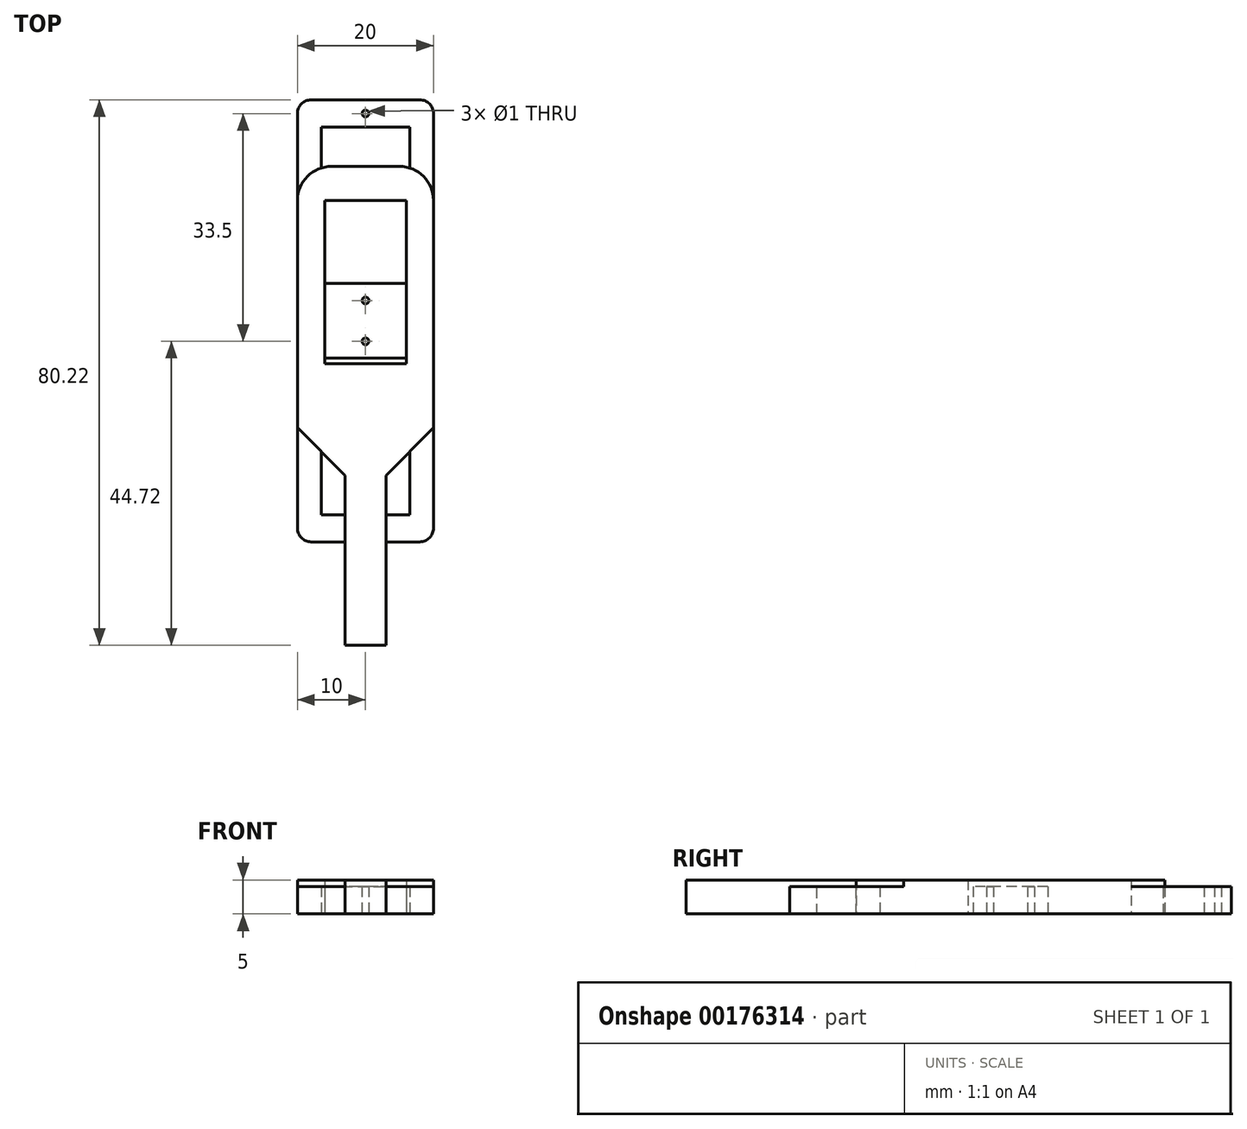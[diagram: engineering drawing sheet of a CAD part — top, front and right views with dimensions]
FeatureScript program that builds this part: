
annotation { "Feature Type Name" : "Feature", "Feature Type Description" : "" }
export const myFeature = defineFeature(function(context is Context, id is Id, definition is map)
    precondition{}
    {
        {
            var Q0;
            Q0=qCreatedBy(makeId("Top.planeOp"),FACE);
            var sketch = newSketch(context, id + "F0", { "sketchPlane" : qUnion([Q0])});
            skLineSegment(sketch, "E0.bottom", {"start": v(-10, -32.5) * mm, "end": v(10, -32.5) * mm});
            skLineSegment(sketch, "E0.top", {"start": v(-10, 32.5) * mm, "end": v(10, 32.5) * mm});
            skLineSegment(sketch, "E0.left", {"start": v(-10, -32.5) * mm, "end": v(-10, 32.5) * mm});
            skLineSegment(sketch, "E0.right", {"start": v(10, -32.5) * mm, "end": v(10, 32.5) * mm});
            skPoint(sketch, "E0.middle", {"position": v(0, 0) * mm});
            skLineSegment(sketch, "E1.bottom", {"start": v(6.5, 28.5) * mm, "end": v(-6.5, 28.5) * mm});
            skLineSegment(sketch, "E1.top", {"start": v(6.5, 5.5) * mm, "end": v(-6.5, 5.5) * mm});
            skLineSegment(sketch, "E1.left", {"start": v(6.5, 28.5) * mm, "end": v(6.5, 5.5) * mm});
            skLineSegment(sketch, "E1.right", {"start": v(-6.5, 28.5) * mm, "end": v(-6.5, 5.5) * mm});
            skPoint(sketch, "E1.middle", {"position": v(0, 17) * mm});
            skLineSegment(sketch, "E2.MirrorCS", {"start": v(6.5, -28.5) * mm, "end": v(-6.5, -28.5) * mm});
            skLineSegment(sketch, "E3.MirrorCS", {"start": v(-6.5, -28.5) * mm, "end": v(-6.5, -5.5) * mm});
            skLineSegment(sketch, "E4.MirrorCS", {"start": v(6.5, -28.5) * mm, "end": v(6.5, -5.5) * mm});
            skLineSegment(sketch, "E5.MirrorCS", {"start": v(6.5, -5.5) * mm, "end": v(-6.5, -5.5) * mm});
            skPoint(sketch, "E6", {"position": v(0, 30.5) * mm});
            skPoint(sketch, "E7", {"position": v(0, 3) * mm});
            skPoint(sketch, "E8", {"position": v(0, -3) * mm});
            skPoint(sketch, "E9", {"position": v(0, -30.5) * mm});
            skPoint(sketch, "E9.positionSnap0", {"position": v(0, -32.5) * mm});
            skCircle(sketch, "E10", {"center": v(0, 30.5) * mm, "radius": 0.5 * mm});
            skCircle(sketch, "E11", {"center": v(0, -30.5) * mm, "radius": 0.5 * mm});
            skCircle(sketch, "E12", {"center": v(0, 3) * mm, "radius": 0.5 * mm});
            skCircle(sketch, "E13", {"center": v(0, -3) * mm, "radius": 0.5 * mm});
            skSolve(sketch);
        }
        {
            var Q0;
            Q0=qSketchRegion(id+"F0",true);
            extrude(context, id + "F1", {"entities" : qUnion([Q0]), "depth" : 4 * mm});
        }
        {
            var Q0;
            Q0=makeQuery(id+"F1.opExtrude","SWEPT_EDGE",EDGE,{"disambiguationData":[OSD([sQuery(id+"F0.wireOp",EDGE,"E0.bottom"),sQuery(id+"F0.wireOp",EDGE,"E0.right")])]});
            var Q1;
            Q1=makeQuery(id+"F1.opExtrude","SWEPT_EDGE",EDGE,{"disambiguationData":[OSD([sQuery(id+"F0.wireOp",EDGE,"E0.top"),sQuery(id+"F0.wireOp",EDGE,"E0.right")])]});
            var Q2;
            Q2=makeQuery(id+"F1.opExtrude","SWEPT_EDGE",EDGE,{"disambiguationData":[OSD([sQuery(id+"F0.wireOp",EDGE,"E0.bottom"),sQuery(id+"F0.wireOp",EDGE,"E0.left")])]});
            var Q3;
            Q3=makeQuery(id+"F1.opExtrude","SWEPT_EDGE",EDGE,{"disambiguationData":[OSD([sQuery(id+"F0.wireOp",EDGE,"E0.top"),sQuery(id+"F0.wireOp",EDGE,"E0.left")])]});
            fillet(context, id + "F2", {"entities" : qUnion([Q0, Q1, Q2, Q3]), "radius" : 2 * mm, "tangentPropagation" : true, "allowEdgeOverflow" : false});
        }
        {
            var Q0;
            Q0=qCreatedBy(makeId("Top.planeOp"),FACE);
            var sketch = newSketch(context, id + "F3", { "sketchPlane" : qUnion([Q0])});
            skLineSegment(sketch, "E14.bottom", {"start": v(-10, -22.72) * mm, "end": v(10, -22.72) * mm});
            skLineSegment(sketch, "E14.top", {"start": v(-10, 22.72) * mm, "end": v(10, 22.72) * mm});
            skLineSegment(sketch, "E14.left", {"start": v(-10, -22.72) * mm, "end": v(-10, 22.72) * mm});
            skLineSegment(sketch, "E14.right", {"start": v(10, -22.72) * mm, "end": v(10, 22.72) * mm});
            skPoint(sketch, "E14.middle", {"position": v(0, 0) * mm});
            skLineSegment(sketch, "E15.bottom", {"start": v(-6, -6.28) * mm, "end": v(6, -6.28) * mm});
            skLineSegment(sketch, "E15.top", {"start": v(-6, 17.72) * mm, "end": v(6, 17.72) * mm});
            skLineSegment(sketch, "E15.left", {"start": v(-6, -6.28) * mm, "end": v(-6, 17.72) * mm});
            skLineSegment(sketch, "E15.right", {"start": v(6, -6.28) * mm, "end": v(6, 17.72) * mm});
            skPoint(sketch, "E15.middle", {"position": v(0, 5.72) * mm});
            skPoint(sketch, "E16", {"position": v(0, 20.22) * mm});
            skPoint(sketch, "E16.positionSnap0", {"position": v(0, 22.72) * mm});
            skPoint(sketch, "E17", {"position": v(0, -22.72) * mm});
            skSolve(sketch);
        }
        {
            var Q0;
            Q0=makeQuery(id+"F3.imprint","IMPRINT",FACE,{"disambiguationData":[TD([[makeQuery(id+"F3.imprint","IMPRINT",EDGE,{"derivedFrom":sQuery(id+"F3.wireOp",EDGE,"E14.bottom")}),1.0]])]});
            extrude(context, id + "F4", {"entities" : qUnion([Q0]), "depth" : 5 * mm});
        }
        {
            var Q0;
            Q0=makeQuery(id+"F4.opExtrude","SWEPT_EDGE",EDGE,{"disambiguationData":[OSD([sQuery(id+"F3.wireOp",EDGE,"E14.bottom"),sQuery(id+"F3.wireOp",EDGE,"E14.left")])]});
            var Q1;
            Q1=makeQuery(id+"F4.opExtrude","SWEPT_EDGE",EDGE,{"disambiguationData":[OSD([sQuery(id+"F3.wireOp",EDGE,"E14.bottom"),sQuery(id+"F3.wireOp",EDGE,"E14.right")])]});
            chamfer(context, id + "F5", {"entities" : qUnion([Q0, Q1]), "width" : 7 * mm, "tangentPropagation" : true});
        }
        {
            var Q0;
            Q0=makeQuery(id+"F4.opExtrude","SWEPT_FACE",FACE,{"disambiguationData":[OSD([sQuery(id+"F3.wireOp",EDGE,"E14.bottom")])]});
            extrude(context, id + "F6", {"entities" : qUnion([Q0]), "operationType" : NewBodyOperationType.ADD, "depth" : 25 * mm});
        }
        {
            var Q0;
            Q0=makeQuery(id+"F4.opExtrude","SWEPT_EDGE",EDGE,{"disambiguationData":[OSD([sQuery(id+"F3.wireOp",EDGE,"E14.top"),sQuery(id+"F3.wireOp",EDGE,"E14.right")])]});
            var Q1;
            Q1=makeQuery(id+"F4.opExtrude","SWEPT_EDGE",EDGE,{"disambiguationData":[OSD([sQuery(id+"F3.wireOp",EDGE,"E14.top"),sQuery(id+"F3.wireOp",EDGE,"E14.left")])]});
            fillet(context, id + "F7", {"entities" : qUnion([Q0, Q1]), "radius" : 5 * mm, "tangentPropagation" : true, "allowEdgeOverflow" : false});
        }
    });
